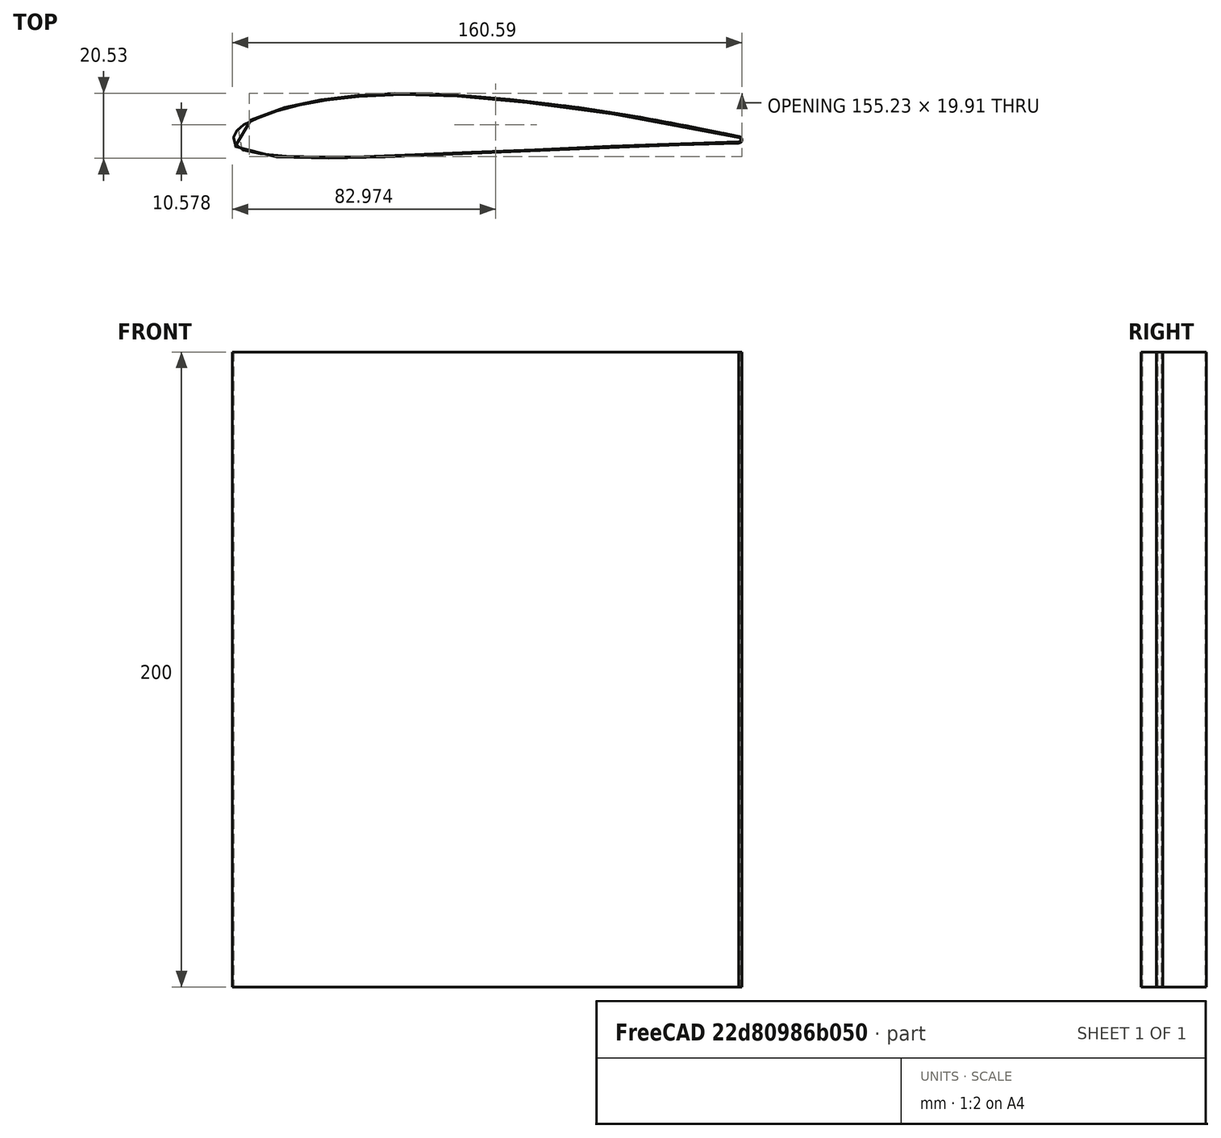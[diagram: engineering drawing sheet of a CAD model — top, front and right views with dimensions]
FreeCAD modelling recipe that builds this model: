
FCSTD DOCUMENT  (FreeCAD 0.21R33694 (Git))
Label: wing
License: All rights reserved
LicenseURL: https://en.wikipedia.org/wiki/All_rights_reserved
objects: Sketcher::SketchObject×2, PartDesign::Pad×2, PartDesign::Body×2, Image::ImagePlane×1, PartDesign::Thickness×1
note: 10 computed .brp shape members not serialized (recipe doc carries the construction recipe); baked Part::Feature solids carry a one-line shape summary decoded from their .brp

FEATURE [Image::ImagePlane] Screenshot_from_2023_09_17_14_32_16  label="Screenshot from 2023-09-17 14-32-16"
  XSize = 164.233
  YSize = 29.0321
FEATURE [Sketcher::SketchObject] Sketch
  FullyConstrained = false
  MapMode = 5
  Support = -> [XY_Plane]
  sketch-geometry (30):
    g0: ArcOfCircle CenterX=78.0455 CenterY=-4.69261 CenterZ=0 NormalX=0 NormalY=0 NormalZ=1 AngleXU=0 Radius=0.633228 StartAngle=4.68069 EndAngle=7.80443
    g1-g15: Circle x15 (B-spline internal-alignment scaffolding for g16; pole/knot coordinates omitted)
    g16: BSplineCurve PolesCount=15 KnotsCount=13 Degree=3 IsPeriodic=0
    g17-g29: GeomPoint x13 (B-spline internal-alignment scaffolding for g16; pole/knot coordinates omitted)
  constraints (6):
    c: Weight(g1) = 1
    c: Coincident(g16,g0)
    c: Equal(g1, g2-g15) x14
    c: Coincident(g16,g0)
    c: InternalAlignment(g1-g15 -> g16) x15
    c: InternalAlignment(g17-g29 -> g16) x13
FEATURE [PartDesign::Pad] Pad
  Direction = (0,0,1)
  Length = 200
  Length2 = 10
  Profile = -> Sketch
  ReferenceAxis = -> Sketch [N_Axis]
  Type = 0
FEATURE [Sketcher::SketchObject] Sketch001
  FullyConstrained = false
  MapMode = 5
  Support = -> [XY_Plane001]
  sketch-geometry (30):
    g0: ArcOfCircle CenterX=78.0455 CenterY=-4.69261 CenterZ=0 NormalX=0 NormalY=0 NormalZ=1 AngleXU=0 Radius=0.633228 StartAngle=4.68069 EndAngle=7.80443
    g1-g15: Circle x15 (B-spline internal-alignment scaffolding for g16; pole/knot coordinates omitted)
    g16: BSplineCurve PolesCount=15 KnotsCount=13 Degree=3 IsPeriodic=0
    g17-g29: GeomPoint x13 (B-spline internal-alignment scaffolding for g16; pole/knot coordinates omitted)
  constraints (6):
    c: Weight(g1) = 1
    c: Coincident(g16,g0)
    c: Equal(g1, g2-g15) x14
    c: Coincident(g16,g0)
    c: InternalAlignment(g1-g15 -> g16) x15
    c: InternalAlignment(g17-g29 -> g16) x13
FEATURE [PartDesign::Pad] Pad001
  Direction = (0,0,1)
  Length = 200
  Length2 = 10
  Profile = -> Sketch001
  ReferenceAxis = -> Sketch001 [N_Axis]
  Type = 0
FEATURE [PartDesign::Body] Body001
  Group = -> [Sketch001,Pad001]
  Origin = -> Origin001
  Tip = -> Pad001
FEATURE [PartDesign::Thickness] Thickness
  Base = -> Pad [Face4,Face3]
  BaseFeature = -> Pad
  Intersection = false
  Join = 0
  Mode = 1
  SupportTransform = false
  Value = 0.4
FEATURE [PartDesign::Body] Body
  Group = -> [Sketch,Pad,Thickness]
  Origin = -> Origin
  Tip = -> Thickness
